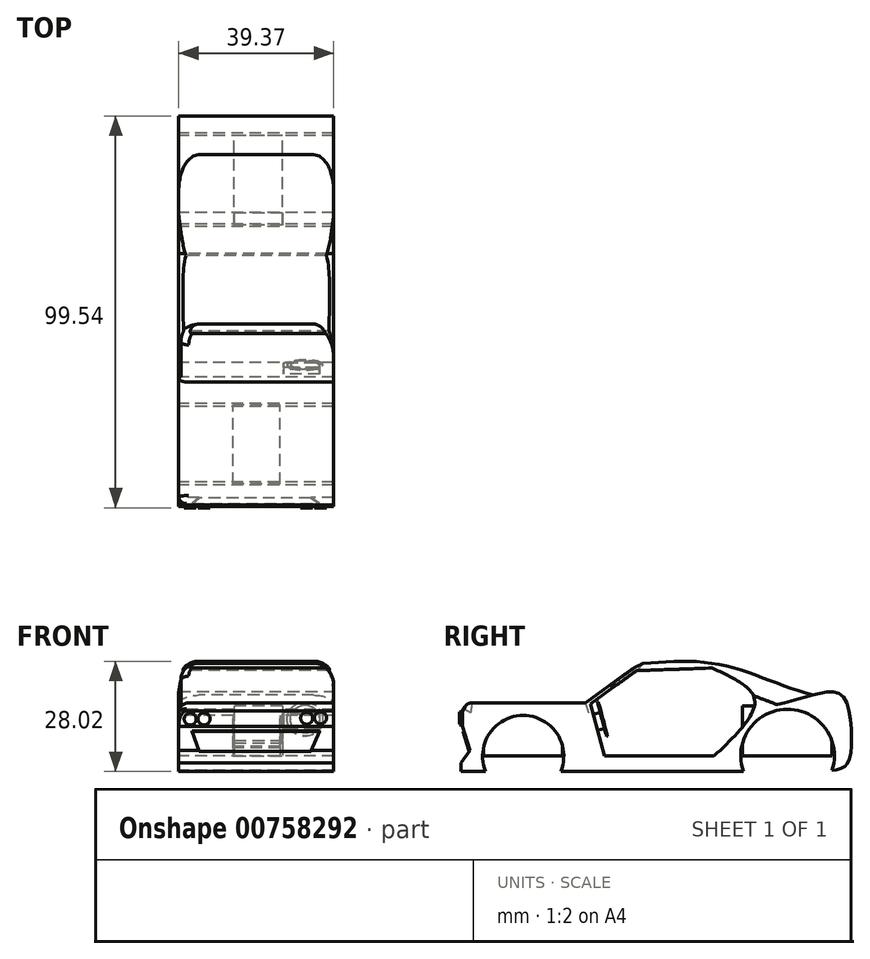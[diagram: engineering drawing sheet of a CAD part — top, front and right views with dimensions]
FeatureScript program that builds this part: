
annotation { "Feature Type Name" : "Feature", "Feature Type Description" : "" }
export const myFeature = defineFeature(function(context is Context, id is Id, definition is map)
    precondition{}
    {
        {
            var Q0;
            Q0=qCreatedBy(makeId("Right.planeOp"),FACE);
            var sketch = newSketch(context, id + "F0", { "sketchPlane" : qUnion([Q0])});
            skFitSpline(sketch, "E0", {"points": [v(-10.45, 23.6) * mm, v(6.76, 23.6) * mm, v(14.38, 21.88) * mm, v(32.57, 15.49) * mm], "startDerivative": vector(96.86, 6.5) * mm, "endDerivative": vector(63.93, -18.58) * mm});
            skFitSpline(sketch, "E1", {"points": [v(32.57, 15.49) * mm, v(39.94, 15.49) * mm, v(42.4, 3.44) * mm, v(40.93, -2.46) * mm, v(37.49, -3.69) * mm], "startDerivative": vector(32.7, 8.7) * mm, "endDerivative": vector(-21.33, -3.46) * mm});
            skCircle(sketch, "E2", {"center": v(26.18, 0) * mm, "radius": 9.1 * mm});
            skArc(sketch, "E3", {"start": v(37.49, -3.69) * mm, "mid": v(26.05, 11.9) * mm, "end": v(14.95, -3.93) * mm});
            skFitSpline(sketch, "E4", {"points": [v(7, 22.37) * mm, v(17.82, 14.26) * mm, v(7.52, 0) * mm], "startDerivative": vector(33.08, -15.17) * mm, "endDerivative": vector(-30.65, -29.26) * mm});
            skLineSegment(sketch, "E5", {"start": v(14.95, -3.93) * mm, "end": v(-20.77, -3.93) * mm});
            skFitSpline(sketch, "E6", {"points": [v(7.52, 0) * mm, v(-20.28, 0) * mm], "startDerivative": vector(-27.8, 0) * mm, "endDerivative": vector(-27.8, 0) * mm});
            skLineSegment(sketch, "E7", {"start": v(-12.9, 22.37) * mm, "end": v(-25.2, 13.52) * mm});
            skLineSegment(sketch, "E8", {"start": v(-25.2, 13.52) * mm, "end": v(-55.18, 13.52) * mm});
            skLineSegment(sketch, "E9", {"start": v(-12.9, 22.37) * mm, "end": v(-10.45, 23.6) * mm});
            skLineSegment(sketch, "E10", {"start": v(7, 22.37) * mm, "end": v(-12.18, 21.7) * mm});
            skLineSegment(sketch, "E11", {"start": v(-12.18, 21.7) * mm, "end": v(-23.87, 13.29) * mm});
            skLineSegment(sketch, "E12", {"start": v(-23.87, 13.29) * mm, "end": v(-20.28, 0) * mm});
            skLineSegment(sketch, "E13", {"start": v(-55.18, 13.52) * mm, "end": v(-56.36, 11.52) * mm});
            skLineSegment(sketch, "E14", {"start": v(-56.36, 11.52) * mm, "end": v(-56.81, 11.52) * mm});
            skLineSegment(sketch, "E15", {"start": v(-56.81, 11.52) * mm, "end": v(-56.81, 7.53) * mm});
            skLineSegment(sketch, "E16", {"start": v(-56.81, 7.53) * mm, "end": v(-56.34, 7.53) * mm});
            skLineSegment(sketch, "E17", {"start": v(-56.34, 7.53) * mm, "end": v(-54.5, 1.38) * mm});
            skLineSegment(sketch, "E18", {"start": v(-54.5, 1.38) * mm, "end": v(-56.81, -1.75) * mm});
            skLineSegment(sketch, "E19", {"start": v(-56.81, -1.75) * mm, "end": v(-56.81, -3.93) * mm});
            skLineSegment(sketch, "E20", {"start": v(-55.52, 0) * mm, "end": v(-55.66, 5.24) * mm});
            skPoint(sketch, "E20.endSnap0", {"position": v(-55.66, -0.19) * mm});
            skLineSegment(sketch, "E21", {"start": v(-56.34, 7.53) * mm, "end": v(-56.36, 11.52) * mm});
            skFitSpline(sketch, "E22", {"points": [v(-46.69, 13.52) * mm, v(-46.24, 16.01) * mm, v(-31.66, 14.57) * mm, v(-29.47, 13.52) * mm], "startDerivative": vector(-3.15, 13.09) * mm, "endDerivative": vector(5.6, -4.27) * mm});
            skCircle(sketch, "E23", {"center": v(-40.98, 0) * mm, "radius": 9.1 * mm});
            skLineSegment(sketch, "E24", {"start": v(-56.81, -3.93) * mm, "end": v(-50.52, -3.93) * mm});
            skArc(sketch, "E25", {"start": v(-50.52, -3.93) * mm, "mid": v(-40.98, 10.32) * mm, "end": v(-31.44, -3.93) * mm});
            skLineSegment(sketch, "E26", {"start": v(-31.44, -3.93) * mm, "end": v(-20.77, -3.93) * mm});
            skSolve(sketch);
        }
        {
            var Q0;
            Q0=makeQuery(id+"F0.imprint","IMPRINT",FACE,{"disambiguationData":[TD([[makeQuery(id+"F0.imprint","IMPRINT",EDGE,{"derivedFrom":sQuery(id+"F0.wireOp",EDGE,"E0")}),-1.0]])]});
            extrude(context, id + "F1", {"entities" : qUnion([Q0]), "depth" : 39.37 * mm, "offsetDistance" : 25.4 * mm});
        }
        {
            var Q0;
            Q0=makeQuery(id+"F1.opExtrude","SWEPT_FACE",FACE,{"disambiguationData":[OSD([sQuery(id+"F0.wireOp",EDGE,"E21")])]});
            var sketch = newSketch(context, id + "F2", { "sketchPlane" : qUnion([Q0])});
            skCircle(sketch, "E27", {"center": v(36.03, 9.97) * mm, "radius": 1.53 * mm});
            skCircle(sketch, "E28", {"center": v(32.51, 9.91) * mm, "radius": 1.53 * mm});
            skCircle(sketch, "E29", {"center": v(6.42, 9.74) * mm, "radius": 1.53 * mm});
            skCircle(sketch, "E30", {"center": v(2.92, 9.7) * mm, "radius": 1.53 * mm});
            skSolve(sketch);
        }
        {
            var Q0;
            Q0=makeQuery(id+"F2.imprint","IMPRINT",FACE,{"disambiguationData":[TD([[makeQuery(id+"F2.imprint","IMPRINT",EDGE,{"derivedFrom":sQuery(id+"F2.wireOp",EDGE,"E30")}),1.0]])]});
            var Q1;
            Q1=makeQuery(id+"F2.imprint","IMPRINT",FACE,{"disambiguationData":[TD([[makeQuery(id+"F2.imprint","IMPRINT",EDGE,{"derivedFrom":sQuery(id+"F2.wireOp",EDGE,"E29")}),1.0]])]});
            var Q2;
            Q2=makeQuery(id+"F2.imprint","IMPRINT",FACE,{"disambiguationData":[TD([[makeQuery(id+"F2.imprint","IMPRINT",EDGE,{"derivedFrom":sQuery(id+"F2.wireOp",EDGE,"E28")}),1.0]])]});
            var Q3;
            Q3=makeQuery(id+"F2.imprint","IMPRINT",FACE,{"disambiguationData":[TD([[makeQuery(id+"F2.imprint","IMPRINT",EDGE,{"derivedFrom":sQuery(id+"F2.wireOp",EDGE,"E27")}),1.0]])]});
            var Q4;
            Q4=sQuery(id+"F2.wireOp",EDGE,"E30");
            var Q5;
            Q5=sQuery(id+"F2.wireOp",EDGE,"E29");
            var Q6;
            Q6=sQuery(id+"F2.wireOp",EDGE,"E28");
            var Q7;
            Q7=sQuery(id+"F2.wireOp",EDGE,"E27");
            extrude(context, id + "F3", {"entities" : qUnion([Q0, Q1, Q2, Q3]), "operationType" : NewBodyOperationType.ADD, "surfaceEntities" : qUnion([Q4, Q5, Q6, Q7]), "depth" : 0.76 * mm, "offsetDistance" : 25.4 * mm});
        }
        {
            var Q0;
            Q0=makeQuery(id+"F1.opExtrude","CAP_EDGE",EDGE,{"disambiguationData":[OSD([sQuery(id+"F0.wireOp",EDGE,"E0")])],"isStart":false});
            var Q1;
            Q1=makeQuery(id+"F1.opExtrude","CAP_EDGE",EDGE,{"disambiguationData":[OSD([sQuery(id+"F0.wireOp",EDGE,"E0")])],"isStart":true});
            fillet(context, id + "F4", {"entities" : qUnion([Q0, Q1]), "radius" : 5.08 * mm, "tangentPropagation" : true, "allowEdgeOverflow" : false});
        }
        {
            var Q0;
            Q0=makeQuery(id+"F1.opExtrude","CAP_EDGE",EDGE,{"disambiguationData":[OSD([sQuery(id+"F0.wireOp",EDGE,"E8")])],"isStart":true});
            var Q1;
            Q1=makeQuery(id+"F1.opExtrude","CAP_EDGE",EDGE,{"disambiguationData":[OSD([sQuery(id+"F0.wireOp",EDGE,"E7")])],"isStart":true});
            fillet(context, id + "F5", {"entities" : qUnion([Q0, Q1]), "radius" : 2.54 * mm, "tangentPropagation" : true, "allowEdgeOverflow" : false});
        }
        {
            var Q0;
            Q0=makeQuery(id+"F1.opExtrude","SWEPT_EDGE",EDGE,{"disambiguationData":[OSD([sQuery(id+"F0.wireOp",EDGE,"E8"),sQuery(id+"F0.wireOp",EDGE,"E13")])]});
            fillet(context, id + "F6", {"entities" : qUnion([Q0]), "radius" : 2.03 * mm, "tangentPropagation" : true, "allowEdgeOverflow" : false});
        }
        {
            var Q0;
            Q0=qCreatedBy(makeId("Top.planeOp"),FACE);
            var sketch = newSketch(context, id + "F7", { "sketchPlane" : qUnion([Q0])});
            skLineSegment(sketch, "E31.bottom", {"start": v(14.06, 14.71) * mm, "end": v(26.34, 14.71) * mm});
            skLineSegment(sketch, "E31.top", {"start": v(14.06, 37.42) * mm, "end": v(26.34, 37.42) * mm});
            skLineSegment(sketch, "E31.left", {"start": v(14.06, 14.71) * mm, "end": v(14.06, 37.42) * mm});
            skLineSegment(sketch, "E31.right", {"start": v(26.34, 14.71) * mm, "end": v(26.34, 37.42) * mm});
            skSolve(sketch);
        }
        {
            var Q0;
            Q0=makeQuery(id+"F7.imprint","IMPRINT",FACE,{"disambiguationData":[TD([[makeQuery(id+"F7.imprint","IMPRINT",EDGE,{"derivedFrom":sQuery(id+"F7.wireOp",EDGE,"E31.bottom")}),1.0]])]});
            var Q1;
            Q1=sQuery(id+"F7.wireOp",EDGE,"E31.right");
            var Q2;
            Q2=sQuery(id+"F7.wireOp",EDGE,"E31.top");
            var Q3;
            Q3=sQuery(id+"F7.wireOp",EDGE,"E31.left");
            var Q4;
            Q4=sQuery(id+"F7.wireOp",EDGE,"E31.bottom");
            extrude(context, id + "F8", {"entities" : qUnion([Q0]), "operationType" : NewBodyOperationType.ADD, "surfaceEntities" : qUnion([Q1, Q2, Q3, Q4]), "depth" : 12.7 * mm, "offsetDistance" : 25.4 * mm});
        }
        {
            var Q0;
            Q0=qCreatedBy(makeId("Top.planeOp"),FACE);
            var sketch = newSketch(context, id + "F9", { "sketchPlane" : qUnion([Q0])});
            skLineSegment(sketch, "E32.bottom", {"start": v(13.85, -51.1) * mm, "end": v(25.77, -51.1) * mm});
            skLineSegment(sketch, "E32.top", {"start": v(13.85, -30.96) * mm, "end": v(25.77, -30.96) * mm});
            skLineSegment(sketch, "E32.left", {"start": v(13.85, -51.1) * mm, "end": v(13.85, -30.96) * mm});
            skLineSegment(sketch, "E32.right", {"start": v(25.77, -51.1) * mm, "end": v(25.77, -30.96) * mm});
            skSolve(sketch);
        }
        {
            var Q0;
            Q0=makeQuery(id+"F9.imprint","IMPRINT",FACE,{"disambiguationData":[TD([[makeQuery(id+"F9.imprint","IMPRINT",EDGE,{"derivedFrom":sQuery(id+"F9.wireOp",EDGE,"E32.bottom")}),1.0]])]});
            var Q1;
            Q1=sQuery(id+"F9.wireOp",EDGE,"E32.left");
            var Q2;
            Q2=sQuery(id+"F9.wireOp",EDGE,"E32.right");
            var Q3;
            Q3=sQuery(id+"F9.wireOp",EDGE,"E32.top");
            var Q4;
            Q4=sQuery(id+"F9.wireOp",EDGE,"E32.bottom");
            extrude(context, id + "F10", {"entities" : qUnion([Q0]), "operationType" : NewBodyOperationType.ADD, "surfaceEntities" : qUnion([Q1, Q2, Q3, Q4]), "depth" : 12.7 * mm, "offsetDistance" : 25.4 * mm});
        }
        {
            var Q0;
            Q0=makeQuery(id+"F1.opExtrude","SWEPT_FACE",FACE,{"disambiguationData":[OSD([sQuery(id+"F0.wireOp",EDGE,"E17")])]});
            var sketch = newSketch(context, id + "F11", { "sketchPlane" : qUnion([Q0])});
            skLineSegment(sketch, "E33", {"start": v(5.22, 16.97) * mm, "end": v(3.4, 22.14) * mm});
            skLineSegment(sketch, "E34", {"start": v(3.4, 22.14) * mm, "end": v(35.78, 22.14) * mm});
            skLineSegment(sketch, "E35", {"start": v(35.78, 22.14) * mm, "end": v(33.57, 16.97) * mm});
            skLineSegment(sketch, "E36", {"start": v(33.57, 16.97) * mm, "end": v(33.57, 16.17) * mm});
            skLineSegment(sketch, "E37", {"start": v(33.57, 16.17) * mm, "end": v(5.17, 16.17) * mm});
            skLineSegment(sketch, "E38", {"start": v(5.17, 16.17) * mm, "end": v(5.22, 16.97) * mm});
            skSolve(sketch);
        }
        {
            var Q0;
            Q0 = qSketchRegion(id + "F11", true);
            extrude(context, id + "F12", {"entities" : qUnion([Q0]), "operationType" : NewBodyOperationType.ADD, "depth" : 0.25 * mm, "offsetDistance" : 25.4 * mm});
        }
        {
            var Q0;
            Q0=makeQuery(id+"F1.opExtrude","SWEPT_FACE",FACE,{"disambiguationData":[OSD([sQuery(id+"F0.wireOp",EDGE,"E12")])]});
            var sketch = newSketch(context, id + "F13", { "sketchPlane" : qUnion([Q0])});
            skLineSegment(sketch, "E39.bottom", {"start": v(-35.82, 16.32) * mm, "end": v(-26.62, 16.32) * mm});
            skLineSegment(sketch, "E39.top", {"start": v(-35.82, 12.11) * mm, "end": v(-26.62, 12.11) * mm});
            skLineSegment(sketch, "E39.left", {"start": v(-35.82, 16.32) * mm, "end": v(-35.82, 12.11) * mm});
            skLineSegment(sketch, "E39.right", {"start": v(-26.62, 16.32) * mm, "end": v(-26.62, 12.11) * mm});
            skSolve(sketch);
        }
        {
            var Q0;
            Q0=makeQuery(id+"F13.imprint","IMPRINT",FACE,{"disambiguationData":[TD([[makeQuery(id+"F13.imprint","IMPRINT",EDGE,{"derivedFrom":sQuery(id+"F13.wireOp",EDGE,"E39.bottom")}),-1.0]])]});
            var Q1;
            Q1=sQuery(id+"F13.wireOp",EDGE,"E39.top");
            var Q2;
            Q2=sQuery(id+"F13.wireOp",EDGE,"E39.left");
            var Q3;
            Q3=sQuery(id+"F13.wireOp",EDGE,"E39.bottom");
            var Q4;
            Q4=sQuery(id+"F13.wireOp",EDGE,"E39.right");
            extrude(context, id + "F14", {"entities" : qUnion([Q0]), "operationType" : NewBodyOperationType.ADD, "surfaceEntities" : qUnion([Q1, Q2, Q3, Q4]), "depth" : 1.78 * mm, "offsetDistance" : 25.4 * mm});
        }
        {
            var Q0;
            Q0=makeQuery(id+"F14.opExtrude","CAP_FACE",FACE,{"disambiguationData":[OSD([sQuery(id+"F13.wireOp",EDGE,"E39.bottom"),sQuery(id+"F13.wireOp",EDGE,"E39.top"),sQuery(id+"F13.wireOp",EDGE,"E39.left"),sQuery(id+"F13.wireOp",EDGE,"E39.right")])],"isStart":false});
            var sketch = newSketch(context, id + "F15", { "sketchPlane" : qUnion([Q0])});
            skCircle(sketch, "E40", {"center": v(-32.05, 14.5) * mm, "radius": 4.51 * mm});
            skCircle(sketch, "E41", {"center": v(-32.05, 14.5) * mm, "radius": 3.68 * mm});
            skSolve(sketch);
        }
        {
            var Q0;
            Q0 = qSketchRegion(id + "F15", true);
            extrude(context, id + "F16", {"entities" : qUnion([Q0]), "operationType" : NewBodyOperationType.ADD, "depth" : 0.25 * mm, "offsetDistance" : 25.4 * mm});
        }
    });
